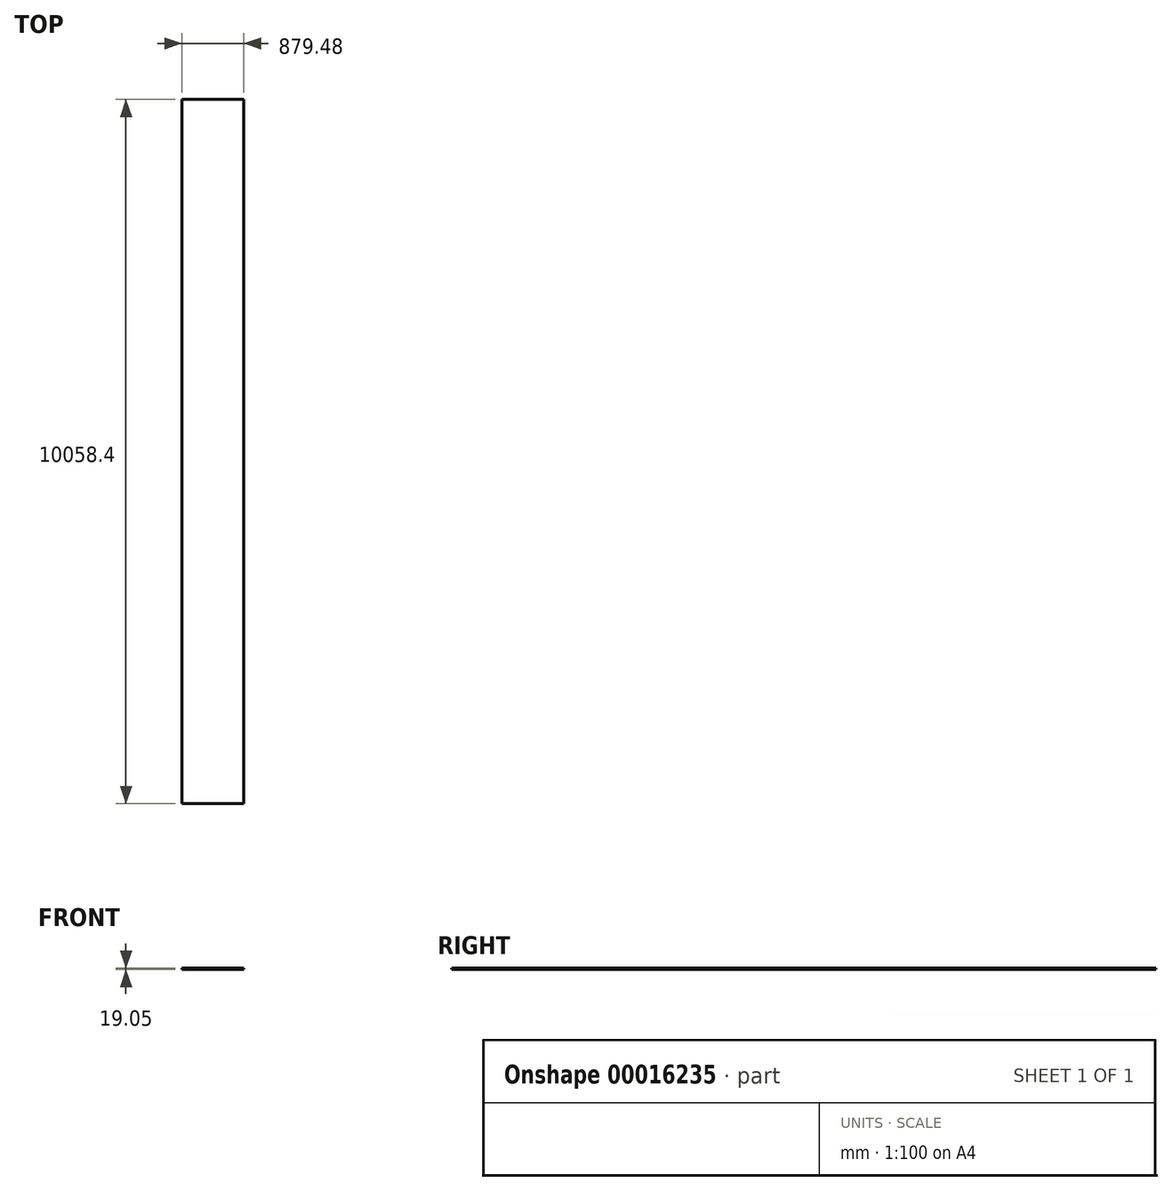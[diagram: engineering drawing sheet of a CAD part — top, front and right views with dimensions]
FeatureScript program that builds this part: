
annotation { "Feature Type Name" : "Feature", "Feature Type Description" : "" }
export const myFeature = defineFeature(function(context is Context, id is Id, definition is map)
    precondition{}
    {
        {
            var Q0;
            Q0=qCreatedBy(makeId("Top.planeOp"),FACE);
            var sketch = newSketch(context, id + "F1", { "sketchPlane" : qUnion([Q0])});
            skLineSegment(sketch, "E0.bottom", {"start": v(-308.4, 45441.85) * mm, "end": v(571.08, 45441.85) * mm});
            skLineSegment(sketch, "E0.top", {"start": v(-308.4, 35383.45) * mm, "end": v(571.08, 35383.45) * mm});
            skLineSegment(sketch, "E0.left", {"start": v(-308.4, 45441.85) * mm, "end": v(-308.4, -278.15) * mm});
            skLineSegment(sketch, "E0.right", {"start": v(571.08, 45441.85) * mm, "end": v(571.08, -278.15) * mm});
            skSolve(sketch);
        }
        {
            var Q0;
            Q0=makeQuery(id+"F1.imprint","IMPRINT",FACE,{"disambiguationData":[TD([[makeQuery(id+"F1.imprint","IMPRINT",EDGE,{"derivedFrom":sQuery(id+"F1.wireOp",EDGE,"E0.bottom")}),-1.0]])]});
            extrude(context, id + "F0", {"entities" : qUnion([Q0]), "oppositeDirection" : true, "depth" : 19.05 * mm});
        }
    });
